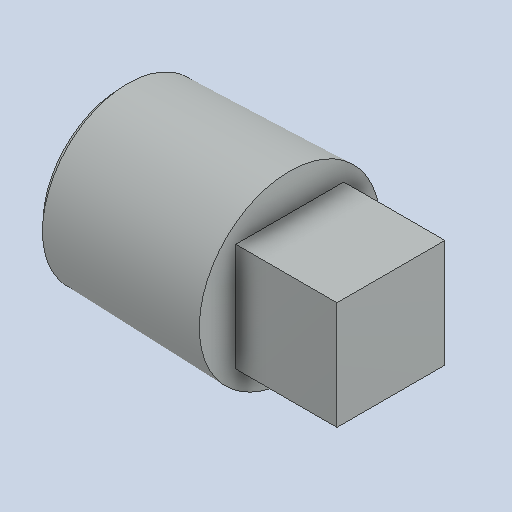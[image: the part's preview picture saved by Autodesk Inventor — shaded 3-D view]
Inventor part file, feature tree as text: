
AUTODESK INVENTOR PART (.ipt)
format: ipt  version: 2024.1 (Build 281209000, 209)  size: 117,248 bytes
history: native  units: in
note: dims shown in document units (in); Inventor stores cm internally (conversion verified against a paired STEP export)
features: chamfer x1
ambient origin geometry x8: Origin, YZ Plane, XZ Plane, XY Plane, X Axis, Y Axis, Z Axis, Center Point
bodies: Solid1 (feature_tree)
feature tree (1):
  chamfer  "Chamfer1"  [1 undecoded]
note: 1 required parameter value undecoded (feature->parameter linkage not recoverable at this tier; creation-order binding heuristic only, values carry confidence <= 0.55)
